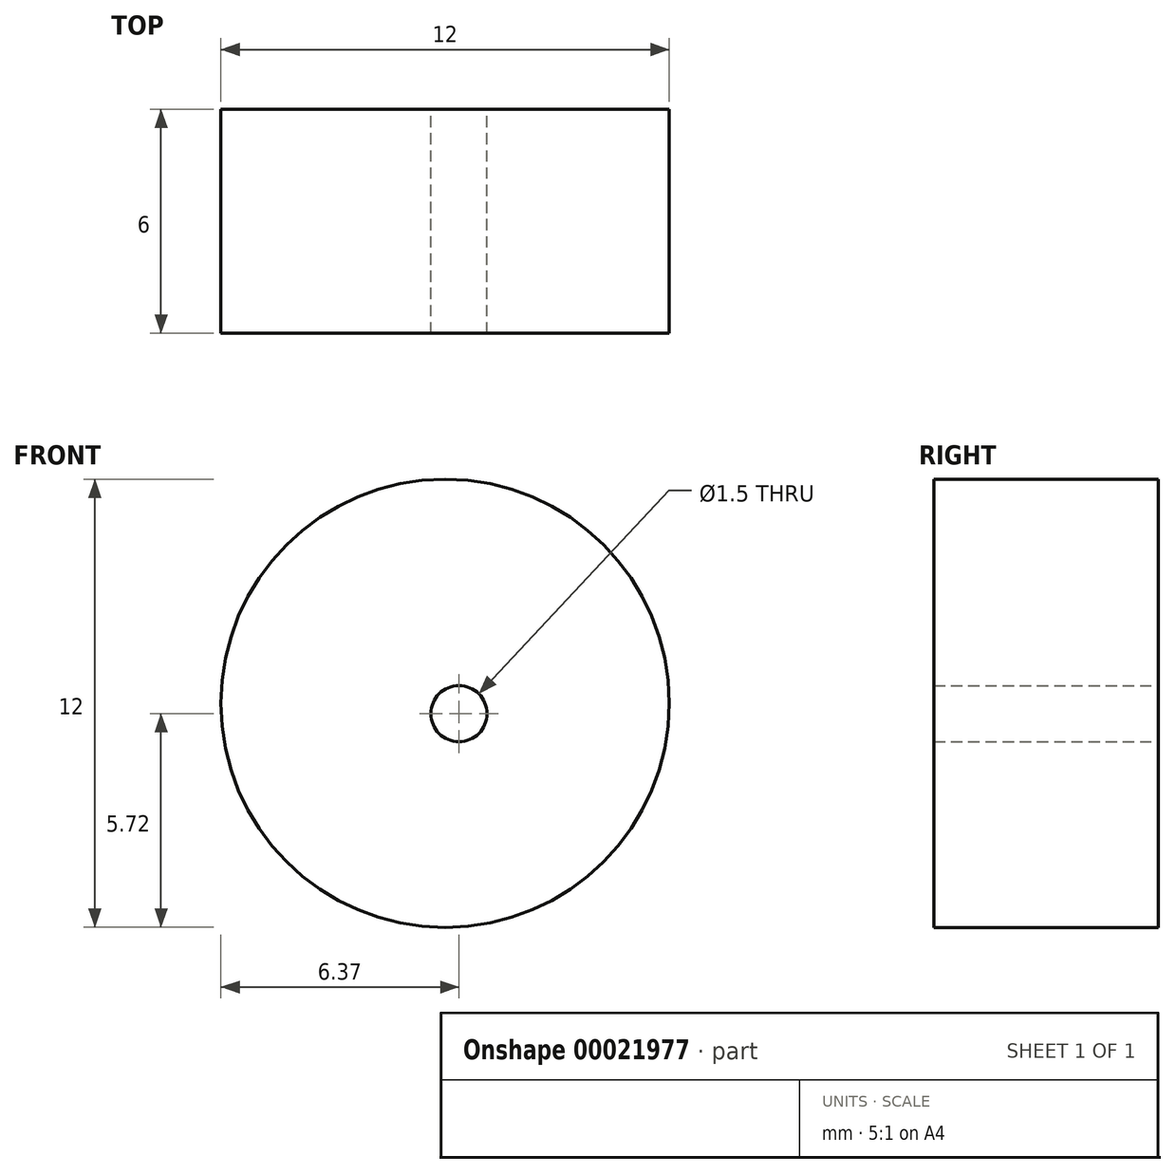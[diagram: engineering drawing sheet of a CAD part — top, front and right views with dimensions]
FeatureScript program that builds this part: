
annotation { "Feature Type Name" : "Feature", "Feature Type Description" : "" }
export const myFeature = defineFeature(function(context is Context, id is Id, definition is map)
    precondition{}
    {
        {
            var Q0;
            Q0=qCreatedBy(makeId("Front.planeOp"),FACE);
            var sketch = newSketch(context, id + "F0", { "sketchPlane" : qUnion([Q0])});
            skCircle(sketch, "E0", {"center": v(-0.37, 0.28) * mm, "radius": 6 * mm});
            skCircle(sketch, "E1", {"center": v(0, 0) * mm, "radius": 0.75 * mm});
            skSolve(sketch);
        }
        {
            var Q0;
            Q0=makeQuery(id+"F0.imprint","IMPRINT",FACE,{"disambiguationData":[TD([[makeQuery(id+"F0.imprint","IMPRINT",EDGE,{"derivedFrom":sQuery(id+"F0.wireOp",EDGE,"E0")}),1.0]])]});
            var Q1;
            Q1=makeQuery(id+"F0.imprint","IMPRINT",FACE,{"disambiguationData":[TD([[makeQuery(id+"F0.imprint","IMPRINT",EDGE,{"derivedFrom":sQuery(id+"F0.wireOp",EDGE,"591e7b63-2bcf-4489-9e5e-a1b71e021af1")}),1.0]])]});
            extrude(context, id + "F1", {"entities" : qUnion([Q0, Q1]), "depth" : 6 * mm});
        }
    });
